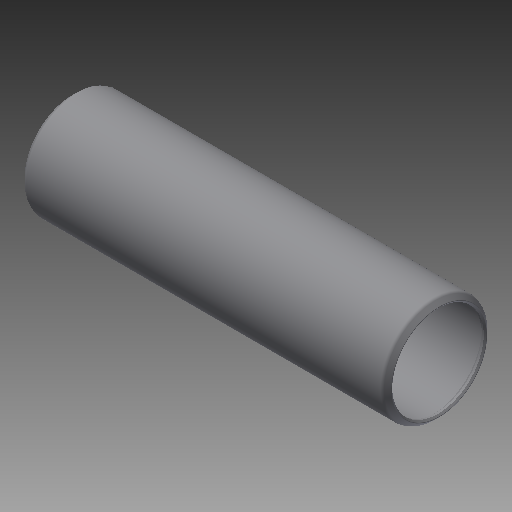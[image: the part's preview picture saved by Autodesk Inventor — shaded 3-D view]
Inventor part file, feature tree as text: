
AUTODESK INVENTOR PART (.ipt)
format: ipt  version: 2019 (Build 230136000, 136)  size: 166,912 bytes
history: native  units: in
note: dims shown in document units (in); Inventor stores cm internally (conversion verified against a paired STEP export)
features: other x42, revolve x1, sketch x1
ambient origin geometry x8: Origin, YZ Plane, XZ Plane, XY Plane, X Axis, Y Axis, Z Axis, Center Point
bodies: Solid1 (feature_tree)
feature tree (44):
  revolve  "Revolution1"  [1 undecoded]
  other  "cp1_XY"
  other  "cp1_YZ"
  other  "cp1_ZX"
  other  "cp1_X"
  other  "cp1_Y"
  other  "cp1_Z"
  other  "cp1_Center"
  other  "cp2_XY"
  other  "cp2_YZ"
  other  "cp2_ZX"
  other  "cp2_X"
  other  "cp2_Y"
  other  "cp2_Z"
  other  "cp2_Center"
  other  "cp3_XY"
  other  "cp3_YZ"
  other  "cp3_ZX"
  other  "cp3_X"
  other  "cp3_Y"
  other  "cp3_Z"
  other  "cp3_Center"
  other  "cp4_XY"
  other  "cp4_YZ"
  other  "cp4_ZX"
  other  "cp4_X"
  other  "cp4_Y"
  other  "cp4_Z"
  other  "cp4_Center"
  other  "tube_front_XY"
  other  "tube_front_YZ"
  other  "tube_front_ZX"
  other  "tube_front_X"
  other  "tube_front_Y"
  other  "tube_front_Z"
  other  "tube_front_Center"
  other  "tube_rear_XY"
  other  "tube_rear_YZ"
  other  "tube_rear_ZX"
  other  "tube_rear_X"
  other  "tube_rear_Y"
  other  "tube_rear_Z"
  other  "tube_rear_Center"
  sketch  "Sketch_1"  dims[d0=360.0deg]
note: 1 required parameter value undecoded (feature->parameter linkage not recoverable at this tier; creation-order binding heuristic only, values carry confidence <= 0.55)
